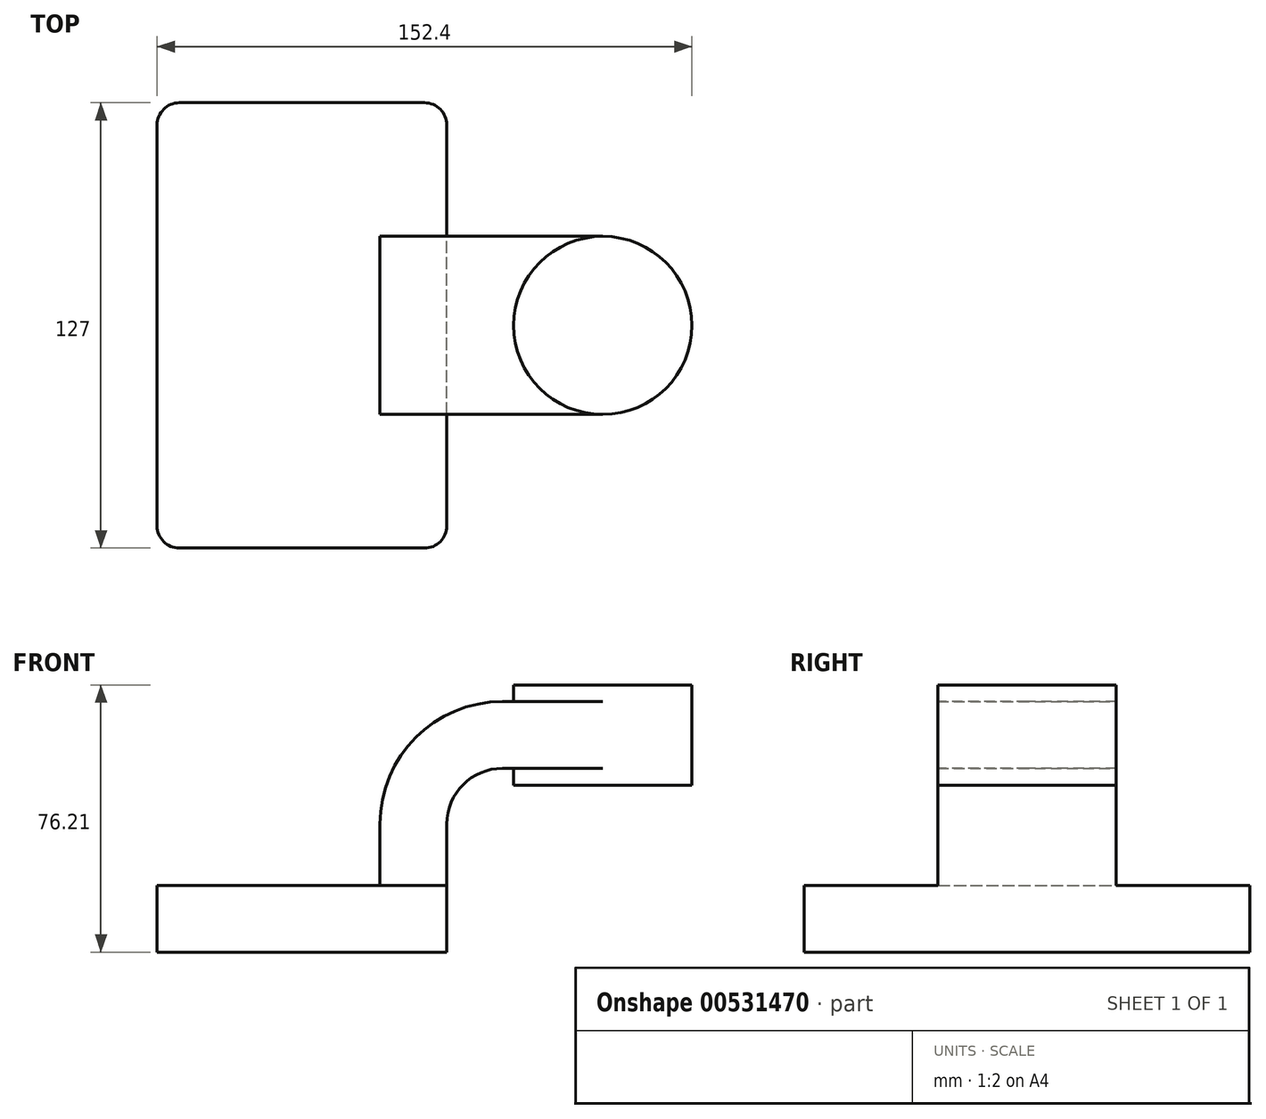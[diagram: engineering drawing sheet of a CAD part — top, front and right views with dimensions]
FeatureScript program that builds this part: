
annotation { "Feature Type Name" : "Feature", "Feature Type Description" : "" }
export const myFeature = defineFeature(function(context is Context, id is Id, definition is map)
    precondition{}
    {
        {
            var Q0;
            Q0=qCreatedBy(makeId("Front.planeOp"),FACE);
            var sketch = newSketch(context, id + "F0", { "sketchPlane" : qUnion([Q0])});
            skLineSegment(sketch, "E0.bottom", {"start": v(-41.28, 9.53) * mm, "end": v(41.28, 9.53) * mm});
            skLineSegment(sketch, "E0.top", {"start": v(-41.28, -9.53) * mm, "end": v(41.28, -9.53) * mm});
            skLineSegment(sketch, "E0.left", {"start": v(-41.28, 9.53) * mm, "end": v(-41.28, -9.53) * mm});
            skLineSegment(sketch, "E0.right", {"start": v(41.28, 9.53) * mm, "end": v(41.28, -9.53) * mm});
            skPoint(sketch, "E0.middle", {"position": v(0, 0) * mm});
            skLineSegment(sketch, "E1.bottom", {"start": v(111.13, 66.68) * mm, "end": v(60.33, 66.68) * mm});
            skLineSegment(sketch, "E1.top", {"start": v(111.13, 38.1) * mm, "end": v(60.33, 38.1) * mm});
            skLineSegment(sketch, "E1.left", {"start": v(111.13, 66.67) * mm, "end": v(111.13, 38.1) * mm});
            skLineSegment(sketch, "E1.right", {"start": v(60.33, 66.67) * mm, "end": v(60.33, 38.1) * mm});
            skPoint(sketch, "E1.middle", {"position": v(85.73, 52.39) * mm});
            skLineSegment(sketch, "E2", {"start": v(41.27, 9.53) * mm, "end": v(41.27, 27) * mm});
            skArc(sketch, "E3", {"start": v(41.28, 27) * mm, "mid": v(45.92, 38.23) * mm, "end": v(57.15, 42.88) * mm});
            skLineSegment(sketch, "E4", {"start": v(57.15, 42.88) * mm, "end": v(85.73, 42.88) * mm});
            skLineSegment(sketch, "E5.0", {"start": v(57.15, 61.93) * mm, "end": v(85.73, 61.93) * mm});
            skArc(sketch, "E5.1", {"start": v(22.23, 27) * mm, "mid": v(32.45, 51.7) * mm, "end": v(57.15, 61.93) * mm});
            skLineSegment(sketch, "E5.2", {"start": v(22.23, 9.53) * mm, "end": v(22.23, 27) * mm});
            skLineSegment(sketch, "E6", {"start": v(85.73, 38.1) * mm, "end": v(85.73, 66.68) * mm});
            skFitSpline(sketch, "E7", {"points": [v(-41.28, 9.53) * mm, v(57.15, 61.93) * mm], "startDerivative": vector(35.5, 108.16) * mm, "endDerivative": vector(95.56, -4.8) * mm});
            skSolve(sketch);
        }
        {
            var Q0;
            Q0=makeQuery(id+"F0.imprint","IMPRINT",FACE,{"disambiguationData":[TD([[makeQuery(id+"F0.imprint","IMPRINT",EDGE,{"derivedFrom":sQuery(id+"F0.wireOp",EDGE,"E0.top")}),1.0]])]});
            extrude(context, id + "F1", {"entities" : qUnion([Q0]), "endBound" : BoundingType.SYMMETRIC, "depth" : 127 * mm, "offsetDistance" : 25.4 * mm});
        }
        {
            var Q0;
            {var subQ0=sQuery(id+"F0.wireOp",EDGE,"E2");Q0=makeQuery(id+"F0.imprint","IMPRINT",FACE,{"disambiguationData":[TD([[makeQuery(id+"F0.imprint","IMPRINT",EDGE,{"derivedFrom":subQ0}),1.0]])]});}
            var Q1;
            {var subQ0=sQuery(id+"F0.wireOp",EDGE,"E5.0");var subQ1=sQuery(id+"F0.wireOp",EDGE,"E1.right");var subQ2=makeQuery(id+"F0.imprint","INTERSECT",VERTEX,{"derivedFrom":[subQ1,subQ0]});Q1=makeQuery(id+"F0.imprint","IMPRINT",FACE,{"disambiguationData":[TD([[makeQuery(id+"F0.imprint","IMPRINT",EDGE,{"disambiguationData":[TD([[subQ2,-1.0]])],"derivedFrom":subQ1}),1.0]])]});}
            extrude(context, id + "F2", {"entities" : qUnion([Q0, Q1]), "operationType" : NewBodyOperationType.ADD, "endBound" : BoundingType.SYMMETRIC, "depth" : 50.8 * mm, "offsetDistance" : 25.4 * mm});
        }
        {
            var Q0;
            Q0=makeQuery(id+"F0.imprint","IMPRINT",FACE,{"disambiguationData":[TD([[makeQuery(id+"F0.imprint","IMPRINT",EDGE,{"derivedFrom":sQuery(id+"F0.wireOp",EDGE,"E5.1")}),1.0]])]});
            extrude(context, id + "F3", {"entities" : qUnion([Q0]), "operationType" : NewBodyOperationType.ADD, "endBound" : BoundingType.SYMMETRIC, "depth" : 15.88 * mm, "offsetDistance" : 25.4 * mm});
        }
        {
            var Q0;
            Q0=makeQuery(id+"F1.opExtrude","CAP_EDGE",EDGE,{"disambiguationData":[OSD([sQuery(id+"F0.wireOp",EDGE,"E0.right")])],"isStart":false});
            var Q1;
            Q1=makeQuery(id+"F1.opExtrude","CAP_EDGE",EDGE,{"disambiguationData":[OSD([sQuery(id+"F0.wireOp",EDGE,"E0.left")])],"isStart":false});
            var Q2;
            Q2=makeQuery(id+"F1.opExtrude","CAP_EDGE",EDGE,{"disambiguationData":[OSD([sQuery(id+"F0.wireOp",EDGE,"E0.left")])],"isStart":true});
            var Q3;
            Q3=makeQuery(id+"F1.opExtrude","CAP_EDGE",EDGE,{"disambiguationData":[OSD([sQuery(id+"F0.wireOp",EDGE,"E0.right")])],"isStart":true});
            fillet(context, id + "F4", {"entities" : qUnion([Q0, Q1, Q2, Q3]), "radius" : 6.35 * mm, "tangentPropagation" : true, "allowEdgeOverflow" : false});
        }
        {
            var Q0;
            {var subQ4=sQuery(id+"F0.wireOp",EDGE,"E1.left");Q0=makeQuery(id+"F0.imprint","IMPRINT",FACE,{"disambiguationData":[TD([[makeQuery(id+"F0.imprint","IMPRINT",EDGE,{"derivedFrom":subQ4}),-1.0]])]});}
            var Q1;
            Q1=sQuery(id+"F0.wireOp",EDGE,"E6");
            revolve(context, id + "F5", {"operationType" : NewBodyOperationType.ADD, "entities" : qUnion([Q0]), "axis" : qUnion([Q1]), "revolveType" : RevolveType.FULL});
        }
    });
